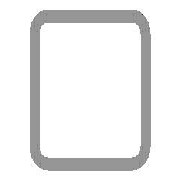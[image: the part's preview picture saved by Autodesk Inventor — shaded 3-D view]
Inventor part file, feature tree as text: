
AUTODESK INVENTOR PART (.ipt)
format: ipt  version: 2025.3 (Build 293356030, 356C)  size: 147,968 bytes
history: native  units: mm (DEFAULTED — no unit token found)
features: other x4, plane x3, split x2, sketch x1
ambient origin geometry x8: Origin, YZ Plane, XZ Plane, XY Plane, X Axis, Y Axis, Z Axis, Center Point
bodies: Solid1 (feature_tree), Body (feature_tree)
feature tree (10):
  parser-record x1  (decoder bookkeeping rows leaked as tree rows — omitted from the tree; the rows remain in map.json)
  other  "Driven Length"
  other  "Start Plane"
  other  "End Plane"
  plane  "Work Plane4"
  split  "Split1"
  plane  "Work Plane5"
  split  "Split2"
  sketch  "Sketch3"  dims[d3=2986.24836mm d4=0.0mm d7=6.0mm d9=60.0mm d11=60.0mm d12=3.0mm d13=133.333333mm d14=3119.581693mm d15=30.0mm d16=30.0mm d17=90.0deg d18=2986.24836mm]
  plane  "Work Plane3"
